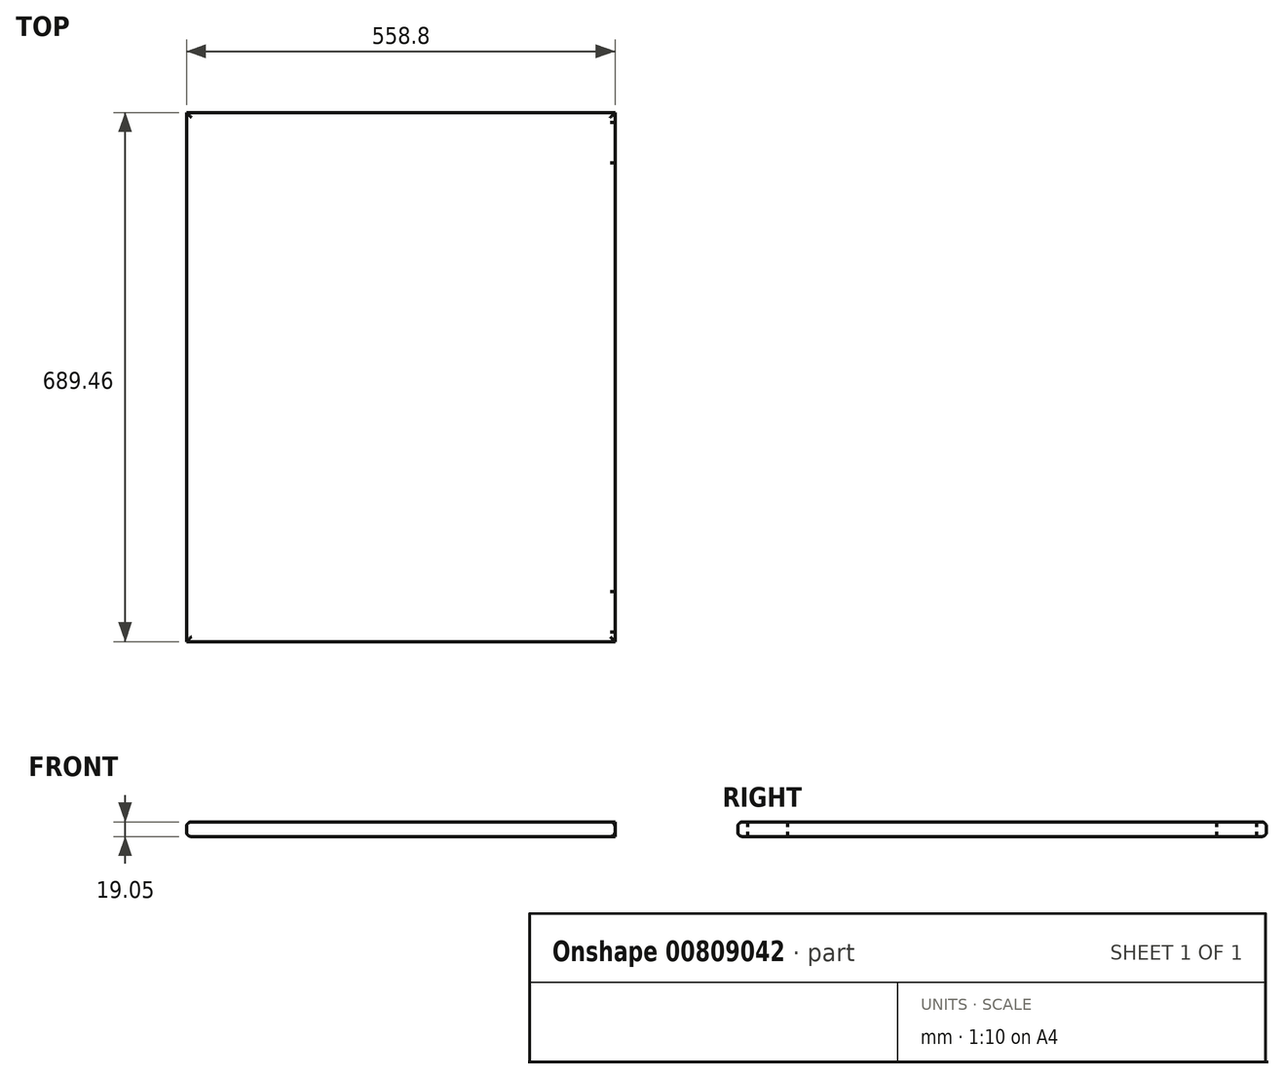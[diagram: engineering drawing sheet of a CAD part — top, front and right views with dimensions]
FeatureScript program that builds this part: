
annotation { "Feature Type Name" : "Feature", "Feature Type Description" : "" }
export const myFeature = defineFeature(function(context is Context, id is Id, definition is map)
    precondition{}
    {
        {
            var Q0;
            Q0=qCreatedBy(makeId("Top.planeOp"),FACE);
            var sketch = newSketch(context, id + "F0", { "sketchPlane" : qUnion([Q0])});
            skLineSegment(sketch, "E0.bottom", {"start": v(0, 0) * mm, "end": v(558.8, 0) * mm});
            skLineSegment(sketch, "E0.top", {"start": v(0, 689.46) * mm, "end": v(558.8, 689.46) * mm});
            skLineSegment(sketch, "E0.left", {"start": v(0, 0) * mm, "end": v(0, 689.46) * mm});
            skLineSegment(sketch, "E0.right", {"start": v(558.8, 0) * mm, "end": v(558.8, 689.46) * mm});
            skSolve(sketch);
        }
        {
            var Q0;
            Q0 = qSketchRegion(id + "F0", true);
            extrude(context, id + "F1", {"entities" : qUnion([Q0]), "flatOperationType" : FlatOperationType.REMOVE, "depth" : 19.05 * mm, "offsetDistance" : 25.4 * mm, "domain" : OperationDomain.MODEL});
        }
        {
            var Q0;
            Q0=makeQuery(id+"F1.opExtrude","CAP_EDGE",EDGE,{"disambiguationData":[OSD([sQuery(id+"F0.wireOp",EDGE,"E0.left")])],"isStart":false});
            var Q1;
            Q1=makeQuery(id+"F1.opExtrude","CAP_EDGE",EDGE,{"disambiguationData":[OSD([sQuery(id+"F0.wireOp",EDGE,"E0.left")])],"isStart":true});
            var Q2;
            Q2=makeQuery(id+"F1.opExtrude","CAP_EDGE",EDGE,{"disambiguationData":[OSD([sQuery(id+"F0.wireOp",EDGE,"E0.bottom")])],"isStart":false});
            var Q3;
            Q3=makeQuery(id+"F1.opExtrude","CAP_EDGE",EDGE,{"disambiguationData":[OSD([sQuery(id+"F0.wireOp",EDGE,"E0.bottom")])],"isStart":true});
            var Q4;
            Q4=makeQuery(id+"F1.opExtrude","SWEPT_EDGE",EDGE,{"disambiguationData":[OSD([sQuery(id+"F0.wireOp",EDGE,"E0.bottom"),sQuery(id+"F0.wireOp",EDGE,"E0.left")])]});
            var Q5;
            Q5=makeQuery(id+"F1.opExtrude","SWEPT_EDGE",EDGE,{"disambiguationData":[OSD([sQuery(id+"F0.wireOp",EDGE,"E0.bottom"),sQuery(id+"F0.wireOp",EDGE,"E0.right")])]});
            var Q6;
            Q6=makeQuery(id+"F1.opExtrude","CAP_EDGE",EDGE,{"disambiguationData":[OSD([sQuery(id+"F0.wireOp",EDGE,"E0.right")])],"isStart":false});
            var Q7;
            Q7=makeQuery(id+"F1.opExtrude","CAP_EDGE",EDGE,{"disambiguationData":[OSD([sQuery(id+"F0.wireOp",EDGE,"E0.right")])],"isStart":true});
            var Q8;
            Q8=makeQuery(id+"F1.opExtrude","SWEPT_EDGE",EDGE,{"disambiguationData":[OSD([sQuery(id+"F0.wireOp",EDGE,"E0.top"),sQuery(id+"F0.wireOp",EDGE,"E0.right")])]});
            var Q9;
            Q9=makeQuery(id+"F1.opExtrude","CAP_EDGE",EDGE,{"disambiguationData":[OSD([sQuery(id+"F0.wireOp",EDGE,"E0.top")])],"isStart":false});
            var Q10;
            Q10=makeQuery(id+"F1.opExtrude","CAP_EDGE",EDGE,{"disambiguationData":[OSD([sQuery(id+"F0.wireOp",EDGE,"E0.top")])],"isStart":true});
            var Q11;
            Q11=makeQuery(id+"F1.opExtrude","SWEPT_EDGE",EDGE,{"disambiguationData":[OSD([sQuery(id+"F0.wireOp",EDGE,"E0.top"),sQuery(id+"F0.wireOp",EDGE,"E0.left")])]});
            fillet(context, id + "F2", {"entities" : qUnion([Q0, Q1, Q2, Q3, Q4, Q5, Q6, Q7, Q8, Q9, Q10, Q11]), "radius" : 6.35 * mm, "tangentPropagation" : true, "allowEdgeOverflow" : false});
        }
        {
            var Q0;
            Q0=makeQuery(id+"F1.opExtrude","SWEPT_FACE",FACE,{"disambiguationData":[OSD([sQuery(id+"F0.wireOp",EDGE,"E0.right")])]});
            var sketch = newSketch(context, id + "F3", { "sketchPlane" : qUnion([Q0])});
            skLineSegment(sketch, "E1.bottom", {"start": v(12.7, 0) * mm, "end": v(65.28, 0) * mm});
            skLineSegment(sketch, "E1.top", {"start": v(12.7, 19.05) * mm, "end": v(65.28, 19.05) * mm});
            skLineSegment(sketch, "E1.left", {"start": v(12.7, 0) * mm, "end": v(12.7, 19.05) * mm});
            skLineSegment(sketch, "E1.right", {"start": v(65.28, 0) * mm, "end": v(65.28, 19.05) * mm});
            skLineSegment(sketch, "E2.bottom", {"start": v(676.76, 0) * mm, "end": v(624.18, 0) * mm});
            skLineSegment(sketch, "E2.top", {"start": v(676.76, 19.05) * mm, "end": v(624.18, 19.05) * mm});
            skLineSegment(sketch, "E2.left", {"start": v(676.76, 0) * mm, "end": v(676.76, 19.05) * mm});
            skLineSegment(sketch, "E2.right", {"start": v(624.18, 0) * mm, "end": v(624.18, 19.05) * mm});
            skSolve(sketch);
        }
        {
            var Q0;
            Q0 = qSketchRegion(id + "F3", true);
            extrude(context, id + "F4", {"entities" : qUnion([Q0]), "operationType" : NewBodyOperationType.ADD, "oppositeDirection" : true, "depth" : 457.2 * mm, "offsetDistance" : 25.4 * mm});
        }
        {
            var Q0;
            Q0 = qSketchRegion(id + "F0", true);
            extrude(context, id + "F5", {"entities" : qUnion([Q0]), "depth" : 19.05 * mm, "offsetDistance" : 25.4 * mm});
        }
        {
            var Q0;
            Q0=makeQuery(id+"F5.opExtrude","CAP_FACE",FACE,{"disambiguationData":[OSD([sQuery(id+"F0.wireOp",EDGE,"E0.bottom"),sQuery(id+"F0.wireOp",EDGE,"E0.top"),sQuery(id+"F0.wireOp",EDGE,"E0.left"),sQuery(id+"F0.wireOp",EDGE,"E0.right")])],"isStart":false});
            var Q1;
            Q1=makeQuery(id+"F5.opExtrude","CAP_EDGE",EDGE,{"disambiguationData":[OSD([sQuery(id+"F0.wireOp",EDGE,"E0.bottom")])],"isStart":true});
            var Q2;
            Q2=makeQuery(id+"F5.opExtrude","CAP_EDGE",EDGE,{"disambiguationData":[OSD([sQuery(id+"F0.wireOp",EDGE,"E0.right")])],"isStart":true});
            var Q3;
            Q3=makeQuery(id+"F5.opExtrude","CAP_FACE",FACE,{"disambiguationData":[OSD([sQuery(id+"F0.wireOp",EDGE,"E0.bottom"),sQuery(id+"F0.wireOp",EDGE,"E0.top"),sQuery(id+"F0.wireOp",EDGE,"E0.left"),sQuery(id+"F0.wireOp",EDGE,"E0.right")])],"isStart":true});
            fillet(context, id + "F6", {"entities" : qUnion([Q0, Q1, Q2, Q3]), "radius" : 6.35 * mm, "tangentPropagation" : true, "allowEdgeOverflow" : false});
        }
    });
